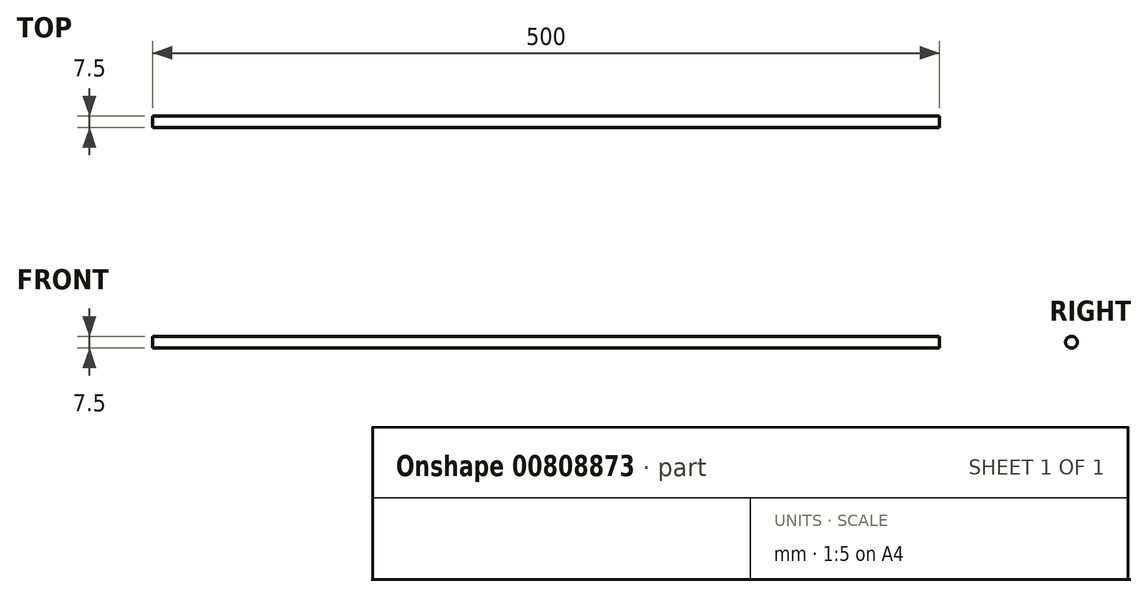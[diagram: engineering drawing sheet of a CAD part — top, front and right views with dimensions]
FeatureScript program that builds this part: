
annotation { "Feature Type Name" : "Feature", "Feature Type Description" : "" }
export const myFeature = defineFeature(function(context is Context, id is Id, definition is map)
    precondition{}
    {
        {
            var Q0;
            Q0=qCreatedBy(makeId("Right.planeOp"),FACE);
            var sketch = newSketch(context, id + "F0", { "sketchPlane" : qUnion([Q0])});
            skCircle(sketch, "E0", {"center": v(0, 0) * mm, "radius": 3.75 * mm});
            skSolve(sketch);
        }
        {
            var Q0;
            Q0=makeQuery(id+"F0.imprint","IMPRINT",FACE,{"disambiguationData":[TD([[makeQuery(id+"F0.imprint","IMPRINT",EDGE,{"derivedFrom":sQuery(id+"F0.wireOp",EDGE,"E0")}),1.0]])]});
            extrude(context, id + "F1", {"entities" : qUnion([Q0]), "depth" : 500 * mm, "offsetDistance" : 25 * mm});
        }
    });
